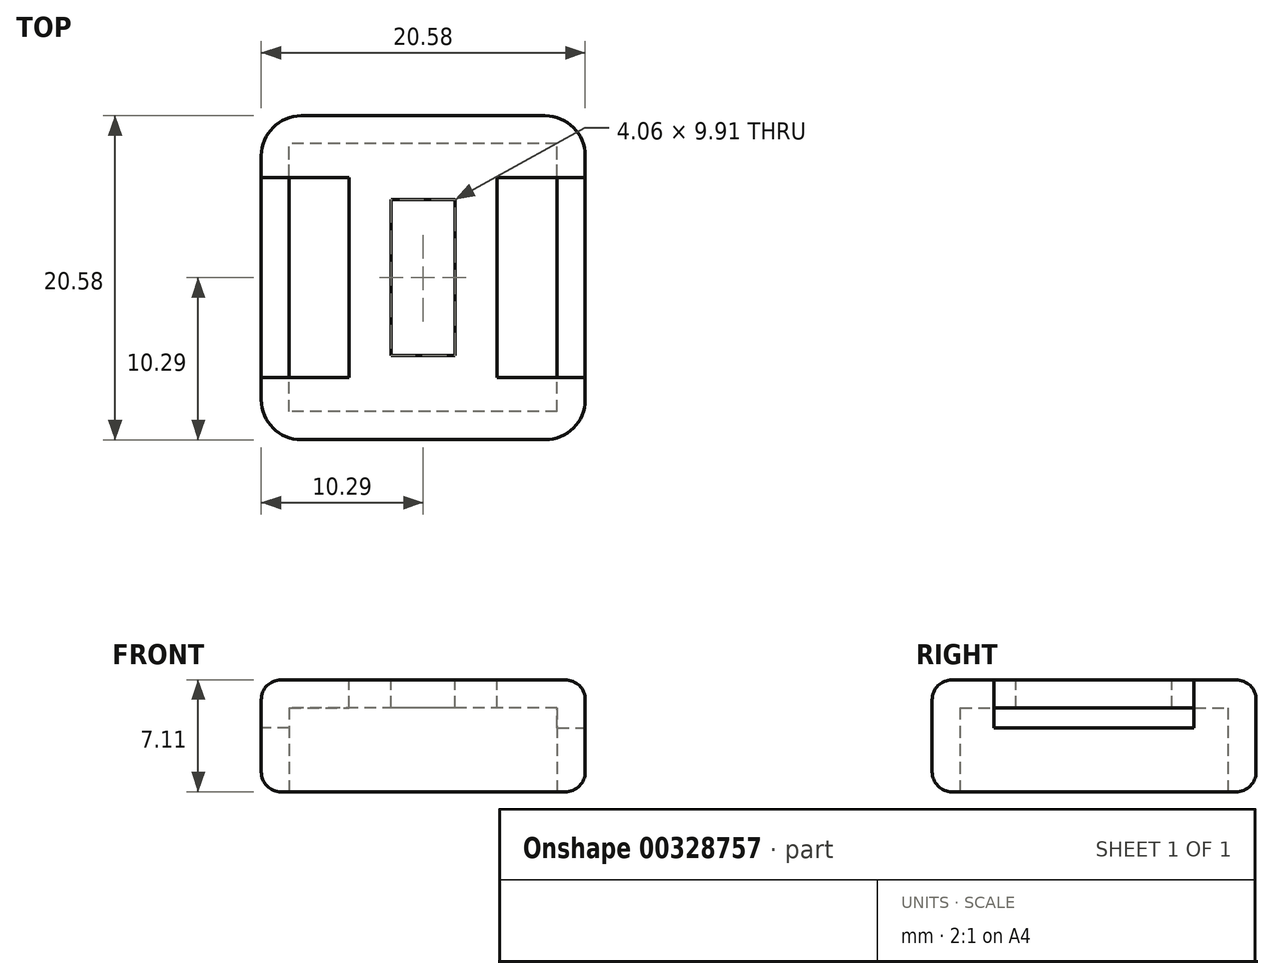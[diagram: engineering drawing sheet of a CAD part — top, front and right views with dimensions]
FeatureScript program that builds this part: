
annotation { "Feature Type Name" : "Feature", "Feature Type Description" : "" }
export const myFeature = defineFeature(function(context is Context, id is Id, definition is map)
    precondition{}
    {
        {
            var Q0;
            Q0=qCreatedBy(makeId("Top.planeOp"),FACE);
            var sketch = newSketch(context, id + "F0", { "sketchPlane" : qUnion([Q0])});
            skLineSegment(sketch, "E0.bottom", {"start": v(10.29, 10.29) * mm, "end": v(-10.29, 10.29) * mm});
            skLineSegment(sketch, "E0.top", {"start": v(10.29, -10.29) * mm, "end": v(-10.29, -10.29) * mm});
            skLineSegment(sketch, "E0.left", {"start": v(10.29, 10.29) * mm, "end": v(10.29, -10.29) * mm});
            skLineSegment(sketch, "E0.right", {"start": v(-10.29, 10.29) * mm, "end": v(-10.29, -10.29) * mm});
            skPoint(sketch, "E0.middle", {"position": v(0, 0) * mm});
            skSolve(sketch);
        }
        {
            var Q0;
            Q0=qSketchRegion(id+"F0",true);
            extrude(context, id + "F1", {"entities" : qUnion([Q0]), "depth" : 7.11 * mm});
        }
        {
            var Q0;
            Q0=makeQuery(id+"F1.opExtrude","CAP_FACE",FACE,{"disambiguationData":[OSD([sQuery(id+"F0.wireOp",EDGE,"E0.bottom"),sQuery(id+"F0.wireOp",EDGE,"E0.top"),sQuery(id+"F0.wireOp",EDGE,"E0.left"),sQuery(id+"F0.wireOp",EDGE,"E0.right")])],"isStart":true});
            var sketch = newSketch(context, id + "F2", { "sketchPlane" : qUnion([Q0])});
            skLineSegment(sketch, "E1.bottom", {"start": v(8.5, 8.5) * mm, "end": v(-8.5, 8.5) * mm});
            skLineSegment(sketch, "E1.top", {"start": v(8.5, -8.5) * mm, "end": v(-8.5, -8.5) * mm});
            skLineSegment(sketch, "E1.left", {"start": v(8.5, 8.5) * mm, "end": v(8.5, -8.5) * mm});
            skLineSegment(sketch, "E1.right", {"start": v(-8.5, 8.5) * mm, "end": v(-8.5, -8.5) * mm});
            skPoint(sketch, "E1.middle", {"position": v(0, 0) * mm});
            skSolve(sketch);
        }
        {
            var Q0;
            Q0=makeQuery(id+"F2.imprint","IMPRINT",FACE,{"disambiguationData":[TD([[makeQuery(id+"F2.imprint","IMPRINT",EDGE,{"derivedFrom":sQuery(id+"F2.wireOp",EDGE,"E1.bottom")}),1.0]])]});
            extrude(context, id + "F3", {"entities" : qUnion([Q0]), "operationType" : NewBodyOperationType.REMOVE, "oppositeDirection" : true, "depth" : 5.33 * mm});
        }
        {
            var Q0;
            Q0=makeQuery(id+"F1.opExtrude","SWEPT_EDGE",EDGE,{"disambiguationData":[OSD([sQuery(id+"F0.wireOp",EDGE,"E0.top"),sQuery(id+"F0.wireOp",EDGE,"E0.right")])]});
            var Q1;
            Q1=makeQuery(id+"F1.opExtrude","SWEPT_EDGE",EDGE,{"disambiguationData":[OSD([sQuery(id+"F0.wireOp",EDGE,"E0.bottom"),sQuery(id+"F0.wireOp",EDGE,"E0.left")])]});
            var Q2;
            Q2=makeQuery(id+"F1.opExtrude","SWEPT_EDGE",EDGE,{"disambiguationData":[OSD([sQuery(id+"F0.wireOp",EDGE,"E0.top"),sQuery(id+"F0.wireOp",EDGE,"E0.left")])]});
            var Q3;
            Q3=makeQuery(id+"F1.opExtrude","SWEPT_EDGE",EDGE,{"disambiguationData":[OSD([sQuery(id+"F0.wireOp",EDGE,"E0.bottom"),sQuery(id+"F0.wireOp",EDGE,"E0.right")])]});
            fillet(context, id + "F4", {"entities" : qUnion([Q0, Q1, Q2, Q3]), "radius" : 2.54 * mm, "tangentPropagation" : true, "allowEdgeOverflow" : false});
        }
        {
            var Q0;
            Q0=makeQuery(id+"F1.opExtrude","CAP_FACE",FACE,{"disambiguationData":[OSD([sQuery(id+"F0.wireOp",EDGE,"E0.bottom"),sQuery(id+"F0.wireOp",EDGE,"E0.top"),sQuery(id+"F0.wireOp",EDGE,"E0.left"),sQuery(id+"F0.wireOp",EDGE,"E0.right")])],"isStart":false});
            var sketch = newSketch(context, id + "F5", { "sketchPlane" : qUnion([Q0])});
            skLineSegment(sketch, "E2.bottom", {"start": v(-4.7, 6.35) * mm, "end": v(-15.88, 6.35) * mm});
            skLineSegment(sketch, "E2.top", {"start": v(-4.7, -6.35) * mm, "end": v(-15.88, -6.35) * mm});
            skLineSegment(sketch, "E2.left", {"start": v(-4.7, 6.35) * mm, "end": v(-4.7, -6.35) * mm});
            skLineSegment(sketch, "E2.right", {"start": v(-15.88, 6.35) * mm, "end": v(-15.88, -6.35) * mm});
            skPoint(sketch, "E2.middle", {"position": v(-10.29, 0) * mm});
            skSolve(sketch);
        }
        {
            var Q0;
            {var subQ0=sQuery(id+"F5.wireOp",EDGE,"E2.left");Q0=makeQuery(id+"F5.imprint","IMPRINT",FACE,{"disambiguationData":[TD([[makeQuery(id+"F5.imprint","IMPRINT",EDGE,{"derivedFrom":subQ0}),-1.0]])]});}
            extrude(context, id + "F6", {"entities" : qUnion([Q0]), "operationType" : NewBodyOperationType.REMOVE, "oppositeDirection" : true, "depth" : 3.05 * mm});
        }
        {
            var Q0;
            Q0=makeQuery(id+"F1.opExtrude","CAP_FACE",FACE,{"disambiguationData":[OSD([sQuery(id+"F0.wireOp",EDGE,"E0.bottom"),sQuery(id+"F0.wireOp",EDGE,"E0.top"),sQuery(id+"F0.wireOp",EDGE,"E0.left"),sQuery(id+"F0.wireOp",EDGE,"E0.right")])],"isStart":false});
            var sketch = newSketch(context, id + "F7", { "sketchPlane" : qUnion([Q0])});
            skLineSegment(sketch, "E3.bottom", {"start": v(4.7, 6.35) * mm, "end": v(15.88, 6.35) * mm});
            skLineSegment(sketch, "E3.top", {"start": v(4.7, -6.35) * mm, "end": v(15.88, -6.35) * mm});
            skLineSegment(sketch, "E3.left", {"start": v(4.7, 6.35) * mm, "end": v(4.7, -6.35) * mm});
            skLineSegment(sketch, "E3.right", {"start": v(15.88, 6.35) * mm, "end": v(15.88, -6.35) * mm});
            skPoint(sketch, "E3.middle", {"position": v(10.29, 0) * mm});
            skSolve(sketch);
        }
        {
            var Q0;
            Q0=qSketchRegion(id+"F7",true);
            extrude(context, id + "F8", {"entities" : qUnion([Q0]), "operationType" : NewBodyOperationType.REMOVE, "oppositeDirection" : true, "depth" : 3.05 * mm});
        }
        {
            var Q0;
            Q0=makeQuery(id+"F1.opExtrude","CAP_FACE",FACE,{"disambiguationData":[OSD([sQuery(id+"F0.wireOp",EDGE,"E0.bottom"),sQuery(id+"F0.wireOp",EDGE,"E0.top"),sQuery(id+"F0.wireOp",EDGE,"E0.left"),sQuery(id+"F0.wireOp",EDGE,"E0.right")])],"isStart":false});
            var sketch = newSketch(context, id + "F9", { "sketchPlane" : qUnion([Q0])});
            skLineSegment(sketch, "E4.bottom", {"start": v(2.03, 4.95) * mm, "end": v(-2.03, 4.95) * mm});
            skLineSegment(sketch, "E4.top", {"start": v(2.03, -4.95) * mm, "end": v(-2.03, -4.95) * mm});
            skLineSegment(sketch, "E4.left", {"start": v(2.03, 4.95) * mm, "end": v(2.03, -4.95) * mm});
            skLineSegment(sketch, "E4.right", {"start": v(-2.03, 4.95) * mm, "end": v(-2.03, -4.95) * mm});
            skPoint(sketch, "E4.middle", {"position": v(0, 0) * mm});
            skSolve(sketch);
        }
        {
            var Q0;
            Q0=qSketchRegion(id+"F9",true);
            extrude(context, id + "F10", {"entities" : qUnion([Q0]), "operationType" : NewBodyOperationType.REMOVE, "oppositeDirection" : true, "depth" : 1.78 * mm});
        }
        {
            var Q0;
            Q0=makeQuery(id+"F1.opExtrude","CAP_EDGE",EDGE,{"disambiguationData":[OSD([sQuery(id+"F0.wireOp",EDGE,"E0.bottom")])],"isStart":false});
            var Q1;
            Q1=makeQuery(id+"F1.opExtrude","CAP_EDGE",EDGE,{"disambiguationData":[OSD([sQuery(id+"F0.wireOp",EDGE,"E0.top")])],"isStart":false});
            fillet(context, id + "F11", {"entities" : qUnion([Q0, Q1]), "radius" : 1.27 * mm, "tangentPropagation" : true, "allowEdgeOverflow" : false});
        }
        {
            var Q0;
            Q0=makeQuery(id+"F1.opExtrude","CAP_EDGE",EDGE,{"disambiguationData":[OSD([sQuery(id+"F0.wireOp",EDGE,"E0.right")])],"isStart":true});
            var Q1;
            Q1=makeQuery(id+"F1.opExtrude","CAP_EDGE",EDGE,{"disambiguationData":[OSD([sQuery(id+"F0.wireOp",EDGE,"E0.bottom")])],"isStart":true});
            var Q2;
            {var subQ0=sQuery(id+"F0.wireOp",EDGE,"E0.right");var subQ1=sQuery(id+"F0.wireOp",EDGE,"E0.bottom");Q2=makeQuery(id+"F4.opFillet","BLEND_EDGE",EDGE,{"blendedFrom":[makeQuery(id+"F1.opExtrude","SWEPT_EDGE",EDGE,{"disambiguationData":[OSD([subQ1,subQ0])]}),makeQuery(id+"F1.opExtrude","CAP_FACE",FACE,{"disambiguationData":[OSD([subQ1,sQuery(id+"F0.wireOp",EDGE,"E0.top"),sQuery(id+"F0.wireOp",EDGE,"E0.left"),subQ0])],"isStart":true})],"blendedInto":[makeQuery(id+"F1.opExtrude","CAP_FACE",FACE,{"disambiguationData":[OSD([subQ1,sQuery(id+"F0.wireOp",EDGE,"E0.top"),sQuery(id+"F0.wireOp",EDGE,"E0.left"),subQ0])],"isStart":true})]});}
            fillet(context, id + "F12", {"entities" : qUnion([Q0, Q1, Q2]), "radius" : 1.27 * mm, "tangentPropagation" : true, "allowEdgeOverflow" : false});
        }
    });
